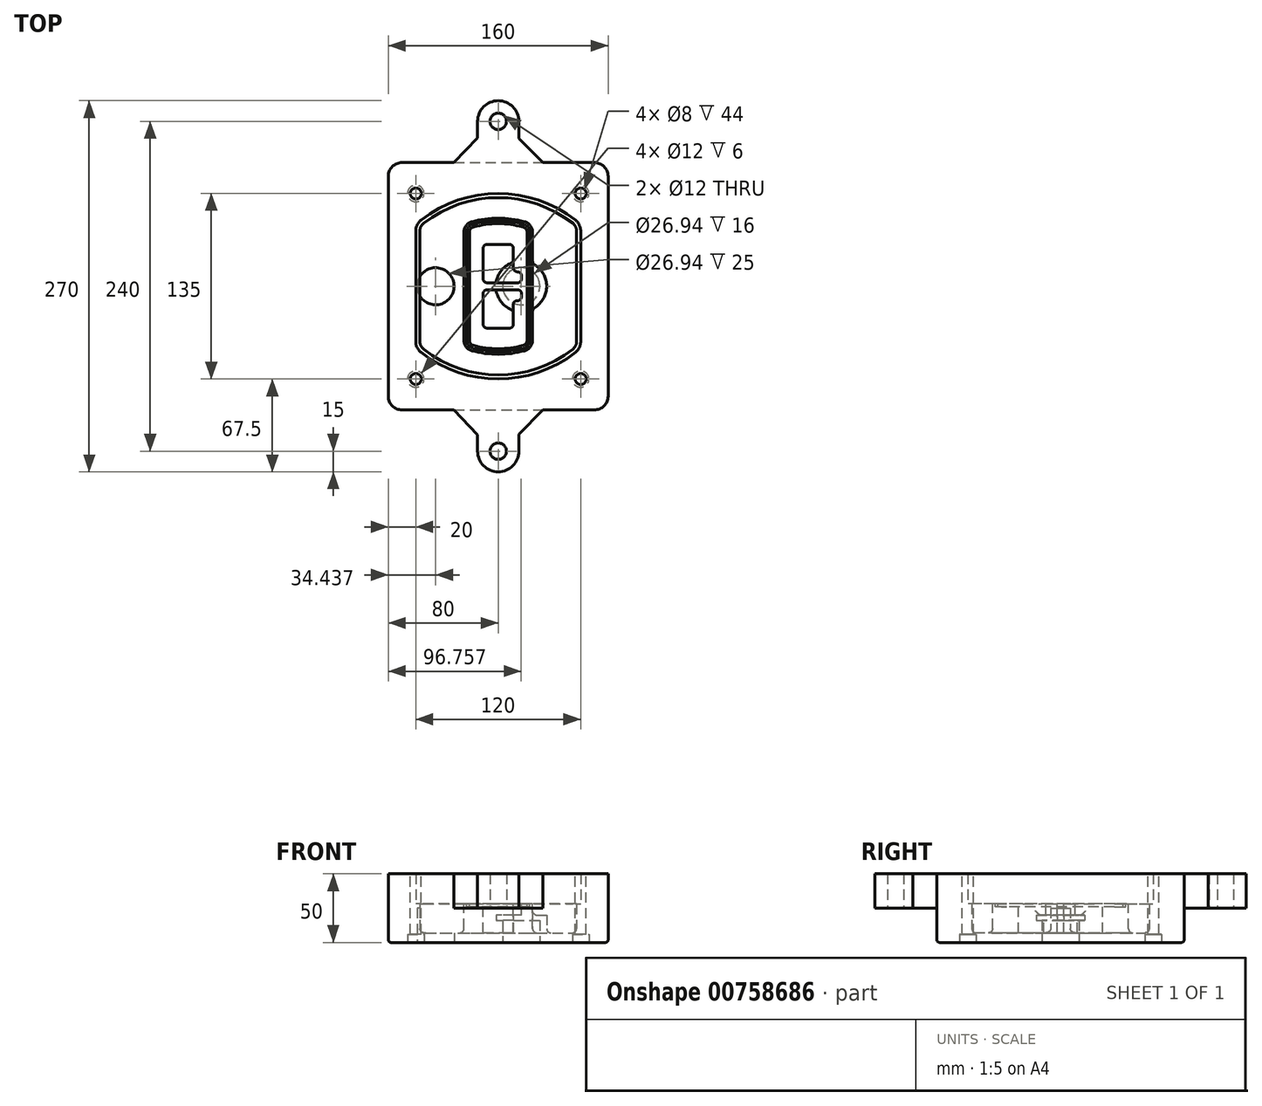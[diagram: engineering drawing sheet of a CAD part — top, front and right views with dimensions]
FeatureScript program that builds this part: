
annotation { "Feature Type Name" : "Feature", "Feature Type Description" : "" }
export const myFeature = defineFeature(function(context is Context, id is Id, definition is map)
    precondition{}
    {
        {
            var Q0;
            Q0=qCreatedBy(makeId("Top.planeOp"),FACE);
            var sketch = newSketch(context, id + "F0", { "sketchPlane" : qUnion([Q0])});
            skPoint(sketch, "E0.rect.middle", {"position": v(0, 0) * mm});
            skLineSegment(sketch, "E1.bottom", {"start": v(-70, -90) * mm, "end": v(70, -90) * mm});
            skLineSegment(sketch, "E1.top", {"start": v(-70, 90) * mm, "end": v(70, 90) * mm});
            skLineSegment(sketch, "E1.left", {"start": v(-80, -80) * mm, "end": v(-80, 80) * mm});
            skLineSegment(sketch, "E1.right", {"start": v(80, -80) * mm, "end": v(80, 80) * mm});
            skLineSegment(sketch, "E2", {"start": v(-80, 90) * mm, "end": v(80, -90) * mm, "construction": true});
            skLineSegment(sketch, "E3", {"start": v(80, 90) * mm, "end": v(-80, -90) * mm, "construction": true});
            skCircle(sketch, "E4", {"center": v(-60, 67.5) * mm, "radius": 4 * mm});
            skCircle(sketch, "E5", {"center": v(60, 67.5) * mm, "radius": 4 * mm});
            skCircle(sketch, "E6", {"center": v(60, -67.5) * mm, "radius": 4 * mm});
            skCircle(sketch, "E7", {"center": v(-60, -67.5) * mm, "radius": 4 * mm});
            skLineSegment(sketch, "E8", {"start": v(-60, 67.5) * mm, "end": v(60, 67.5) * mm, "construction": true});
            skLineSegment(sketch, "E9", {"start": v(60, 67.5) * mm, "end": v(60, -67.5) * mm, "construction": true});
            skLineSegment(sketch, "E10", {"start": v(60, -67.5) * mm, "end": v(-60, -67.5) * mm, "construction": true});
            skLineSegment(sketch, "E11", {"start": v(-60, -67.5) * mm, "end": v(-60, 67.5) * mm, "construction": true});
            skLineSegment(sketch, "E12", {"start": v(-60, 40.3) * mm, "end": v(-60, -40.3) * mm});
            skLineSegment(sketch, "E13", {"start": v(60, 40.3) * mm, "end": v(60, -40.3) * mm});
            skArc(sketch, "E14", {"start": v(56.15, 48.18) * mm, "mid": v(0, 67.5) * mm, "end": v(-56.15, 48.18) * mm});
            skArc(sketch, "E15", {"start": v(-56.15, -48.18) * mm, "mid": v(0, -67.5) * mm, "end": v(56.15, -48.18) * mm});
            skLineSegment(sketch, "E16", {"start": v(-60, 0) * mm, "end": v(60, 0) * mm, "construction": true});
            skPoint(sketch, "E17.visualSharp", {"position": v(-60, -45) * mm});
            skArc(sketch, "E17.filletArc", {"start": v(-60, -40.3) * mm, "mid": v(-58.99, -44.68) * mm, "end": v(-56.15, -48.18) * mm});
            skPoint(sketch, "E18.visualSharp", {"position": v(-60, 45) * mm});
            skArc(sketch, "E18.filletArc", {"start": v(-56.15, 48.18) * mm, "mid": v(-58.99, 44.68) * mm, "end": v(-60, 40.3) * mm});
            skPoint(sketch, "E19.visualSharp", {"position": v(60, 45) * mm});
            skArc(sketch, "E19.filletArc", {"start": v(60, 40.3) * mm, "mid": v(58.99, 44.68) * mm, "end": v(56.15, 48.18) * mm});
            skPoint(sketch, "E20.visualSharp", {"position": v(60, -45) * mm});
            skArc(sketch, "E20.filletArc", {"start": v(56.15, -48.18) * mm, "mid": v(58.99, -44.68) * mm, "end": v(60, -40.3) * mm});
            skPoint(sketch, "E21.visualSharp", {"position": v(-80, 90) * mm});
            skArc(sketch, "E21.filletArc", {"start": v(-70, 90) * mm, "mid": v(-77.07, 87.07) * mm, "end": v(-80, 80) * mm});
            skPoint(sketch, "E22.visualSharp", {"position": v(80, 90) * mm});
            skArc(sketch, "E22.filletArc", {"start": v(80, 80) * mm, "mid": v(77.07, 87.07) * mm, "end": v(70, 90) * mm});
            skPoint(sketch, "E23.visualSharp", {"position": v(80, -90) * mm});
            skArc(sketch, "E23.filletArc", {"start": v(70, -90) * mm, "mid": v(77.07, -87.07) * mm, "end": v(80, -80) * mm});
            skPoint(sketch, "E24.visualSharp", {"position": v(-80, -90) * mm});
            skArc(sketch, "E24.filletArc", {"start": v(-80, -80) * mm, "mid": v(-77.07, -87.07) * mm, "end": v(-70, -90) * mm});
            skArc(sketch, "E25.0", {"start": v(57, 40.3) * mm, "mid": v(56.3, 43.36) * mm, "end": v(54.3, 45.81) * mm});
            skLineSegment(sketch, "E25.1", {"start": v(57, 40.3) * mm, "end": v(57, -40.3) * mm});
            skArc(sketch, "E25.2", {"start": v(54.3, -45.81) * mm, "mid": v(56.3, -43.36) * mm, "end": v(57, -40.3) * mm});
            skArc(sketch, "E25.3", {"start": v(-54.3, -45.81) * mm, "mid": v(0, -64.5) * mm, "end": v(54.3, -45.81) * mm});
            skArc(sketch, "E25.4", {"start": v(-57, -40.3) * mm, "mid": v(-56.3, -43.36) * mm, "end": v(-54.3, -45.81) * mm});
            skArc(sketch, "E25.5", {"start": v(54.3, 45.81) * mm, "mid": v(0, 64.5) * mm, "end": v(-54.3, 45.81) * mm});
            skLineSegment(sketch, "E25.6", {"start": v(-57, 40.3) * mm, "end": v(-57, -40.3) * mm});
            skArc(sketch, "E25.7", {"start": v(-54.3, 45.81) * mm, "mid": v(-56.3, 43.36) * mm, "end": v(-57, 40.3) * mm});
            skArc(sketch, "E26.0", {"start": v(-58.62, 51.33) * mm, "mid": v(-62.58, 46.43) * mm, "end": v(-64, 40.3) * mm});
            skArc(sketch, "E26.1", {"start": v(58.62, 51.33) * mm, "mid": v(0, 71.5) * mm, "end": v(-58.62, 51.33) * mm});
            skArc(sketch, "E26.2", {"start": v(64, 40.3) * mm, "mid": v(62.58, 46.43) * mm, "end": v(58.62, 51.33) * mm});
            skLineSegment(sketch, "E26.3", {"start": v(64, 40.3) * mm, "end": v(64, -40.3) * mm});
            skArc(sketch, "E26.4", {"start": v(58.62, -51.33) * mm, "mid": v(62.58, -46.43) * mm, "end": v(64, -40.3) * mm});
            skLineSegment(sketch, "E26.5", {"start": v(-64, 40.3) * mm, "end": v(-64, -40.3) * mm});
            skArc(sketch, "E26.6", {"start": v(-58.62, -51.33) * mm, "mid": v(0, -71.5) * mm, "end": v(58.62, -51.33) * mm});
            skArc(sketch, "E26.7", {"start": v(-64, -40.3) * mm, "mid": v(-62.58, -46.43) * mm, "end": v(-58.62, -51.33) * mm});
            skSolve(sketch);
        }
        {
            var Q0;
            Q0=makeQuery(id+"F0.imprint","IMPRINT",FACE,{"disambiguationData":[TD([[makeQuery(id+"F0.imprint","IMPRINT",EDGE,{"derivedFrom":sQuery(id+"F0.wireOp",EDGE,"E1.bottom")}),1.0]])]});
            var Q1;
            Q1=makeQuery(id+"F0.imprint","IMPRINT",FACE,{"disambiguationData":[TD([[makeQuery(id+"F0.imprint","IMPRINT",EDGE,{"derivedFrom":sQuery(id+"F0.wireOp",EDGE,"E12")}),1.0]])]});
            var Q2;
            Q2=makeQuery(id+"F0.imprint","IMPRINT",FACE,{"disambiguationData":[TD([[makeQuery(id+"F0.imprint","IMPRINT",EDGE,{"derivedFrom":sQuery(id+"F0.wireOp",EDGE,"E25.0")}),1.0]])]});
            var Q3;
            Q3=makeQuery(id+"F0.imprint","IMPRINT",FACE,{"disambiguationData":[TD([[makeQuery(id+"F0.imprint","IMPRINT",EDGE,{"derivedFrom":sQuery(id+"F0.wireOp",EDGE,"E12")}),-1.0]])]});
            extrude(context, id + "F1", {"entities" : qUnion([Q0, Q1, Q2, Q3]), "oppositeDirection" : true, "depth" : 25 * mm});
        }
        {
            var Q0;
            Q0=makeQuery(id+"F0.imprint","IMPRINT",FACE,{"disambiguationData":[TD([[makeQuery(id+"F0.imprint","IMPRINT",EDGE,{"derivedFrom":sQuery(id+"F0.wireOp",EDGE,"E12")}),1.0]])]});
            extrude(context, id + "F2", {"entities" : qUnion([Q0]), "operationType" : NewBodyOperationType.ADD, "depth" : 3 * mm});
        }
        {
            var Q0;
            Q0=makeQuery(id+"F0.imprint","IMPRINT",FACE,{"disambiguationData":[TD([[makeQuery(id+"F0.imprint","IMPRINT",EDGE,{"derivedFrom":sQuery(id+"F0.wireOp",EDGE,"E25.0")}),1.0]])]});
            extrude(context, id + "F3", {"entities" : qUnion([Q0]), "operationType" : NewBodyOperationType.REMOVE, "oppositeDirection" : true, "depth" : 18 * mm});
        }
        {
            var Q0;
            Q0=makeQuery(id+"F2.opExtrude","CAP_FACE",FACE,{"disambiguationData":[OSD([sQuery(id+"F0.wireOp",EDGE,"E12"),sQuery(id+"F0.wireOp",EDGE,"E13"),sQuery(id+"F0.wireOp",EDGE,"E14"),sQuery(id+"F0.wireOp",EDGE,"E15"),sQuery(id+"F0.wireOp",EDGE,"E17.filletArc"),sQuery(id+"F0.wireOp",EDGE,"E18.filletArc"),sQuery(id+"F0.wireOp",EDGE,"E19.filletArc"),sQuery(id+"F0.wireOp",EDGE,"E20.filletArc"),sQuery(id+"F0.wireOp",EDGE,"E25.0"),sQuery(id+"F0.wireOp",EDGE,"E25.1"),sQuery(id+"F0.wireOp",EDGE,"E25.2"),sQuery(id+"F0.wireOp",EDGE,"E25.3"),sQuery(id+"F0.wireOp",EDGE,"E25.4"),sQuery(id+"F0.wireOp",EDGE,"E25.5"),sQuery(id+"F0.wireOp",EDGE,"E25.6"),sQuery(id+"F0.wireOp",EDGE,"E25.7")])],"isStart":false});
            var sketch = newSketch(context, id + "F4", { "sketchPlane" : qUnion([Q0])});
            skArc(sketch, "E27.0", {"start": v(-19.08, -46.97) * mm, "mid": v(0, -49.5) * mm, "end": v(19.08, -46.97) * mm});
            skArc(sketch, "E28.0", {"start": v(19.08, 46.97) * mm, "mid": v(0, 49.5) * mm, "end": v(-19.08, 46.97) * mm});
            skLineSegment(sketch, "E29", {"start": v(-25, 39.25) * mm, "end": v(-25, -39.25) * mm});
            skLineSegment(sketch, "E30", {"start": v(25, 39.25) * mm, "end": v(25, -39.25) * mm});
            skLineSegment(sketch, "E31", {"start": v(-25, 45.1) * mm, "end": v(25, 45.1) * mm, "construction": true});
            skLineSegment(sketch, "E32", {"start": v(-25, -45.1) * mm, "end": v(25, -45.1) * mm, "construction": true});
            skPoint(sketch, "E33.visualSharp", {"position": v(-25, 45.1) * mm});
            skArc(sketch, "E33.filletArc", {"start": v(-19.08, 46.97) * mm, "mid": v(-23.35, 44.11) * mm, "end": v(-25, 39.25) * mm});
            skPoint(sketch, "E34.visualSharp", {"position": v(25, 45.1) * mm});
            skArc(sketch, "E34.filletArc", {"start": v(25, 39.25) * mm, "mid": v(23.35, 44.11) * mm, "end": v(19.08, 46.97) * mm});
            skPoint(sketch, "E35.visualSharp", {"position": v(25, -45.1) * mm});
            skArc(sketch, "E35.filletArc", {"start": v(19.08, -46.97) * mm, "mid": v(23.35, -44.11) * mm, "end": v(25, -39.25) * mm});
            skPoint(sketch, "E36.visualSharp", {"position": v(-25, -45.1) * mm});
            skArc(sketch, "E36.filletArc", {"start": v(-25, -39.25) * mm, "mid": v(-23.35, -44.11) * mm, "end": v(-19.08, -46.97) * mm});
            skArc(sketch, "E37.0", {"start": v(54.3, 45.81) * mm, "mid": v(0, 64.5) * mm, "end": v(-54.3, 45.81) * mm});
            skArc(sketch, "E37.1", {"start": v(-54.3, 45.81) * mm, "mid": v(-56.3, 43.36) * mm, "end": v(-57, 40.3) * mm});
            skLineSegment(sketch, "E37.2", {"start": v(-57, 40.3) * mm, "end": v(-57, -40.3) * mm});
            skArc(sketch, "E37.3", {"start": v(-57, -40.3) * mm, "mid": v(-56.3, -43.36) * mm, "end": v(-54.3, -45.81) * mm});
            skArc(sketch, "E37.4", {"start": v(-54.3, -45.81) * mm, "mid": v(0, -64.5) * mm, "end": v(54.3, -45.81) * mm});
            skArc(sketch, "E37.5", {"start": v(54.3, -45.81) * mm, "mid": v(56.3, -43.36) * mm, "end": v(57, -40.3) * mm});
            skLineSegment(sketch, "E37.6", {"start": v(57, 40.3) * mm, "end": v(57, -40.3) * mm});
            skArc(sketch, "E37.7", {"start": v(57, 40.3) * mm, "mid": v(56.3, 43.36) * mm, "end": v(54.3, 45.81) * mm});
            skLineSegment(sketch, "E38.0", {"start": v(23, 39.25) * mm, "end": v(23, -39.25) * mm});
            skArc(sketch, "E38.1", {"start": v(18.56, -45.04) * mm, "mid": v(21.76, -42.9) * mm, "end": v(23, -39.25) * mm});
            skArc(sketch, "E38.2", {"start": v(-18.56, -45.04) * mm, "mid": v(0, -47.5) * mm, "end": v(18.56, -45.04) * mm});
            skArc(sketch, "E38.3", {"start": v(-23, -39.25) * mm, "mid": v(-21.76, -42.9) * mm, "end": v(-18.56, -45.04) * mm});
            skLineSegment(sketch, "E38.4", {"start": v(-23, 39.25) * mm, "end": v(-23, -39.25) * mm});
            skArc(sketch, "E38.5", {"start": v(23, 39.25) * mm, "mid": v(21.76, 42.9) * mm, "end": v(18.56, 45.04) * mm});
            skArc(sketch, "E38.6", {"start": v(-18.56, 45.04) * mm, "mid": v(-21.76, 42.9) * mm, "end": v(-23, 39.25) * mm});
            skArc(sketch, "E38.7", {"start": v(18.56, 45.04) * mm, "mid": v(0, 47.5) * mm, "end": v(-18.56, 45.04) * mm});
            skArc(sketch, "E39.0", {"start": v(21, 39.25) * mm, "mid": v(20.18, 41.68) * mm, "end": v(18.04, 43.1) * mm});
            skLineSegment(sketch, "E39.1", {"start": v(21, 39.25) * mm, "end": v(21, -39.25) * mm});
            skArc(sketch, "E39.2", {"start": v(18.04, -43.1) * mm, "mid": v(20.18, -41.68) * mm, "end": v(21, -39.25) * mm});
            skArc(sketch, "E39.3", {"start": v(-18.04, -43.1) * mm, "mid": v(0, -45.5) * mm, "end": v(18.04, -43.1) * mm});
            skArc(sketch, "E39.4", {"start": v(-21, -39.25) * mm, "mid": v(-20.18, -41.68) * mm, "end": v(-18.04, -43.1) * mm});
            skArc(sketch, "E39.5", {"start": v(18.04, 43.1) * mm, "mid": v(0, 45.5) * mm, "end": v(-18.04, 43.1) * mm});
            skLineSegment(sketch, "E39.6", {"start": v(-21, 39.25) * mm, "end": v(-21, -39.25) * mm});
            skArc(sketch, "E39.7", {"start": v(-18.04, 43.1) * mm, "mid": v(-20.18, 41.68) * mm, "end": v(-21, 39.25) * mm});
            skLineSegment(sketch, "E40", {"start": v(-25, 0) * mm, "end": v(25, 0) * mm, "construction": true});
            skLineSegment(sketch, "E41", {"start": v(-11, 5.5) * mm, "end": v(-11, 27.5) * mm});
            skLineSegment(sketch, "E42", {"start": v(-8, 30.5) * mm, "end": v(8, 30.5) * mm});
            skLineSegment(sketch, "E43", {"start": v(11, 27.5) * mm, "end": v(11, 13.5) * mm});
            skLineSegment(sketch, "E44", {"start": v(14, 10.5) * mm, "end": v(14, 10.5) * mm});
            skLineSegment(sketch, "E45", {"start": v(17, 7.5) * mm, "end": v(17, 5.5) * mm});
            skLineSegment(sketch, "E46", {"start": v(14, 2.5) * mm, "end": v(-8, 2.5) * mm});
            skPoint(sketch, "E47.visualSharp", {"position": v(-11, 30.5) * mm});
            skArc(sketch, "E47.filletArc", {"start": v(-8, 30.5) * mm, "mid": v(-10.12, 29.62) * mm, "end": v(-11, 27.5) * mm});
            skPoint(sketch, "E48.visualSharp", {"position": v(11, 30.5) * mm});
            skArc(sketch, "E48.filletArc", {"start": v(11, 27.5) * mm, "mid": v(10.12, 29.62) * mm, "end": v(8, 30.5) * mm});
            skPoint(sketch, "E49.visualSharp", {"position": v(11, 10.5) * mm});
            skArc(sketch, "E49.filletArc", {"start": v(11, 13.5) * mm, "mid": v(11.88, 11.38) * mm, "end": v(14, 10.5) * mm});
            skPoint(sketch, "E50.visualSharp", {"position": v(17, 10.5) * mm});
            skArc(sketch, "E50.filletArc", {"start": v(17, 7.5) * mm, "mid": v(16.12, 9.62) * mm, "end": v(14, 10.5) * mm});
            skPoint(sketch, "E51.visualSharp", {"position": v(17, 2.5) * mm});
            skArc(sketch, "E51.filletArc", {"start": v(14, 2.5) * mm, "mid": v(16.12, 3.38) * mm, "end": v(17, 5.5) * mm});
            skPoint(sketch, "E52.visualSharp", {"position": v(-11, 2.5) * mm});
            skArc(sketch, "E52.filletArc", {"start": v(-11, 5.5) * mm, "mid": v(-10.12, 3.38) * mm, "end": v(-8, 2.5) * mm});
            skLineSegment(sketch, "E53.0.MirrorCS", {"start": v(14, -2.5) * mm, "end": v(-8, -2.5) * mm});
            skArc(sketch, "E54.0.MirrorCS", {"start": v(-11, -5.5) * mm, "mid": v(-10.12, -3.38) * mm, "end": v(-8, -2.5) * mm});
            skLineSegment(sketch, "E55.0.MirrorCS", {"start": v(-11, -5.5) * mm, "end": v(-11, -27.5) * mm});
            skArc(sketch, "E56.0.MirrorCS", {"start": v(-8, -30.5) * mm, "mid": v(-10.12, -29.62) * mm, "end": v(-11, -27.5) * mm});
            skLineSegment(sketch, "E57.0.MirrorCS", {"start": v(-8, -30.5) * mm, "end": v(8, -30.5) * mm});
            skArc(sketch, "E58.0.MirrorCS", {"start": v(11, -27.5) * mm, "mid": v(10.12, -29.62) * mm, "end": v(8, -30.5) * mm});
            skLineSegment(sketch, "E59.0.MirrorCS", {"start": v(11, -27.5) * mm, "end": v(11, -13.5) * mm});
            skArc(sketch, "E60.0.MirrorCS", {"start": v(11, -13.5) * mm, "mid": v(11.88, -11.38) * mm, "end": v(14, -10.5) * mm});
            skArc(sketch, "E61.0.MirrorCS", {"start": v(17, -7.5) * mm, "mid": v(16.12, -9.62) * mm, "end": v(14, -10.5) * mm});
            skLineSegment(sketch, "E62.0.MirrorCS", {"start": v(17, -7.5) * mm, "end": v(17, -5.5) * mm});
            skArc(sketch, "E63.0.MirrorCS", {"start": v(14, -2.5) * mm, "mid": v(16.12, -3.38) * mm, "end": v(17, -5.5) * mm});
            skSolve(sketch);
        }
        {
            var Q0;
            Q0=makeQuery(id+"F4.imprint","IMPRINT",FACE,{"disambiguationData":[TD([[makeQuery(id+"F4.imprint","IMPRINT",EDGE,{"derivedFrom":sQuery(id+"F4.wireOp",EDGE,"E27.0")}),1.0]])]});
            var Q1;
            Q1=makeQuery(id+"F4.imprint","IMPRINT",FACE,{"disambiguationData":[TD([[makeQuery(id+"F4.imprint","IMPRINT",EDGE,{"derivedFrom":sQuery(id+"F4.wireOp",EDGE,"E38.0")}),-1.0]])]});
            var Q2;
            Q2=makeQuery(id+"F4.imprint","IMPRINT",FACE,{"disambiguationData":[TD([[makeQuery(id+"F4.imprint","IMPRINT",EDGE,{"derivedFrom":sQuery(id+"F4.wireOp",EDGE,"E39.0")}),1.0]])]});
            extrude(context, id + "F5", {"entities" : qUnion([Q0, Q1, Q2]), "operationType" : NewBodyOperationType.ADD, "endBound" : BoundingType.UP_TO_NEXT, "oppositeDirection" : true, "depth" : 25 * mm});
        }
        {
            var Q0;
            Q0=makeQuery(id+"F4.imprint","IMPRINT",FACE,{"disambiguationData":[TD([[makeQuery(id+"F4.imprint","IMPRINT",EDGE,{"derivedFrom":sQuery(id+"F4.wireOp",EDGE,"E38.0")}),-1.0]])]});
            extrude(context, id + "F6", {"entities" : qUnion([Q0]), "operationType" : NewBodyOperationType.REMOVE, "oppositeDirection" : true, "depth" : 2 * mm});
        }
        {
            var Q0;
            Q0=makeQuery(id+"F1.opExtrude","CAP_FACE",FACE,{"disambiguationData":[OSD([sQuery(id+"F0.wireOp",EDGE,"E1.bottom"),sQuery(id+"F0.wireOp",EDGE,"E1.top"),sQuery(id+"F0.wireOp",EDGE,"E1.left"),sQuery(id+"F0.wireOp",EDGE,"E1.right"),sQuery(id+"F0.wireOp",EDGE,"E4"),sQuery(id+"F0.wireOp",EDGE,"E5"),sQuery(id+"F0.wireOp",EDGE,"E6"),sQuery(id+"F0.wireOp",EDGE,"E7"),sQuery(id+"F0.wireOp",EDGE,"E21.filletArc"),sQuery(id+"F0.wireOp",EDGE,"E22.filletArc"),sQuery(id+"F0.wireOp",EDGE,"E23.filletArc"),sQuery(id+"F0.wireOp",EDGE,"E24.filletArc")])],"isStart":false});
            var sketch = newSketch(context, id + "F7", { "sketchPlane" : qUnion([Q0])});
            skCircle(sketch, "E64", {"center": v(16.76, 0) * mm, "radius": 13.47 * mm});
            skCircle(sketch, "E65", {"center": v(-45.56, 0) * mm, "radius": 13.47 * mm});
            skLineSegment(sketch, "E66", {"start": v(80, 0) * mm, "end": v(-80, 0) * mm});
            skCircle(sketch, "E67", {"center": v(16.76, 0) * mm, "radius": 18.47 * mm});
            skCircle(sketch, "E68", {"center": v(60, -67.5) * mm, "radius": 6 * mm});
            skCircle(sketch, "E69", {"center": v(-60, -67.5) * mm, "radius": 6 * mm});
            skCircle(sketch, "E70", {"center": v(-60, 67.5) * mm, "radius": 6 * mm});
            skCircle(sketch, "E71", {"center": v(60, 67.5) * mm, "radius": 6 * mm});
            skSolve(sketch);
        }
        {
            var Q0;
            {var subQ1=sQuery(id+"F7.wireOp",EDGE,"E66");var subQ4=sQuery(id+"F7.wireOp",EDGE,"E64");var subQ6=makeQuery(id+"F7.imprint","INTERSECT",VERTEX,{"disambiguationData":[OD(0.0)],"derivedFrom":[subQ4,subQ1]});Q0=makeQuery(id+"F7.imprint","IMPRINT",FACE,{"disambiguationData":[TD([[makeQuery(id+"F7.imprint","IMPRINT",EDGE,{"disambiguationData":[TD([[subQ6,-1.0]])],"derivedFrom":subQ4}),-1.0]])]});}
            var Q1;
            {var subQ0=sQuery(id+"F7.wireOp",EDGE,"E66");var subQ1=sQuery(id+"F7.wireOp",EDGE,"E64");var subQ3=makeQuery(id+"F7.imprint","INTERSECT",VERTEX,{"disambiguationData":[OD(0.0)],"derivedFrom":[subQ1,subQ0]});Q1=makeQuery(id+"F7.imprint","IMPRINT",FACE,{"disambiguationData":[TD([[makeQuery(id+"F7.imprint","IMPRINT",EDGE,{"disambiguationData":[TD([[subQ3,-1.0]])],"derivedFrom":subQ1}),1.0]])]});}
            var Q2;
            {var subQ0=sQuery(id+"F7.wireOp",EDGE,"E66");var subQ1=sQuery(id+"F7.wireOp",EDGE,"E64");var subQ3=makeQuery(id+"F7.imprint","INTERSECT",VERTEX,{"disambiguationData":[OD(0.0)],"derivedFrom":[subQ1,subQ0]});Q2=makeQuery(id+"F7.imprint","IMPRINT",FACE,{"disambiguationData":[TD([[makeQuery(id+"F7.imprint","IMPRINT",EDGE,{"disambiguationData":[TD([[subQ3,1.0]])],"derivedFrom":subQ1}),1.0]])]});}
            var Q3;
            {var subQ1=sQuery(id+"F7.wireOp",EDGE,"E66");var subQ4=sQuery(id+"F7.wireOp",EDGE,"E64");var subQ6=makeQuery(id+"F7.imprint","INTERSECT",VERTEX,{"disambiguationData":[OD(0.0)],"derivedFrom":[subQ4,subQ1]});Q3=makeQuery(id+"F7.imprint","IMPRINT",FACE,{"disambiguationData":[TD([[makeQuery(id+"F7.imprint","IMPRINT",EDGE,{"disambiguationData":[TD([[subQ6,1.0]])],"derivedFrom":subQ4}),-1.0]])]});}
            extrude(context, id + "F8", {"entities" : qUnion([Q0, Q1, Q2, Q3]), "operationType" : NewBodyOperationType.ADD, "oppositeDirection" : true, "depth" : 20 * mm});
        }
        {
            var Q0;
            {var subQ0=sQuery(id+"F7.wireOp",EDGE,"E66");var subQ1=sQuery(id+"F7.wireOp",EDGE,"E64");var subQ3=makeQuery(id+"F7.imprint","INTERSECT",VERTEX,{"disambiguationData":[OD(0.0)],"derivedFrom":[subQ1,subQ0]});Q0=makeQuery(id+"F7.imprint","IMPRINT",FACE,{"disambiguationData":[TD([[makeQuery(id+"F7.imprint","IMPRINT",EDGE,{"disambiguationData":[TD([[subQ3,-1.0]])],"derivedFrom":subQ1}),1.0]])]});}
            var Q1;
            {var subQ0=sQuery(id+"F7.wireOp",EDGE,"E66");var subQ1=sQuery(id+"F7.wireOp",EDGE,"E64");var subQ3=makeQuery(id+"F7.imprint","INTERSECT",VERTEX,{"disambiguationData":[OD(0.0)],"derivedFrom":[subQ1,subQ0]});Q1=makeQuery(id+"F7.imprint","IMPRINT",FACE,{"disambiguationData":[TD([[makeQuery(id+"F7.imprint","IMPRINT",EDGE,{"disambiguationData":[TD([[subQ3,1.0]])],"derivedFrom":subQ1}),1.0]])]});}
            extrude(context, id + "F9", {"entities" : qUnion([Q0, Q1]), "operationType" : NewBodyOperationType.REMOVE, "oppositeDirection" : true, "depth" : 16 * mm});
        }
        {
            var Q0;
            {var subQ0=sQuery(id+"F7.wireOp",EDGE,"E66");var subQ1=sQuery(id+"F7.wireOp",EDGE,"E65");var subQ3=makeQuery(id+"F7.imprint","INTERSECT",VERTEX,{"disambiguationData":[OD(0.0)],"derivedFrom":[subQ1,subQ0]});Q0=makeQuery(id+"F7.imprint","IMPRINT",FACE,{"disambiguationData":[TD([[makeQuery(id+"F7.imprint","IMPRINT",EDGE,{"disambiguationData":[TD([[subQ3,-1.0]])],"derivedFrom":subQ1}),1.0]])]});}
            var Q1;
            {var subQ0=sQuery(id+"F7.wireOp",EDGE,"E66");var subQ1=sQuery(id+"F7.wireOp",EDGE,"E65");var subQ3=makeQuery(id+"F7.imprint","INTERSECT",VERTEX,{"disambiguationData":[OD(0.0)],"derivedFrom":[subQ1,subQ0]});Q1=makeQuery(id+"F7.imprint","IMPRINT",FACE,{"disambiguationData":[TD([[makeQuery(id+"F7.imprint","IMPRINT",EDGE,{"disambiguationData":[TD([[subQ3,1.0]])],"derivedFrom":subQ1}),1.0]])]});}
            extrude(context, id + "F10", {"entities" : qUnion([Q0, Q1]), "operationType" : NewBodyOperationType.REMOVE, "oppositeDirection" : true, "depth" : 25 * mm});
        }
        {
            var Q0;
            Q0=makeQuery(id+"F7.imprint","IMPRINT",FACE,{"disambiguationData":[TD([[makeQuery(id+"F7.imprint","IMPRINT",EDGE,{"derivedFrom":sQuery(id+"F7.wireOp",EDGE,"E68")}),1.0]])]});
            var Q1;
            Q1=makeQuery(id+"F7.imprint","IMPRINT",FACE,{"disambiguationData":[TD([[makeQuery(id+"F7.imprint","IMPRINT",EDGE,{"derivedFrom":makeQuery(id+"F1.opExtrude","CAP_EDGE",EDGE,{"disambiguationData":[OSD([sQuery(id+"F0.wireOp",EDGE,"E5")])],"isStart":false})}),-1.0]])]});
            var Q2;
            Q2=makeQuery(id+"F7.imprint","IMPRINT",FACE,{"disambiguationData":[TD([[makeQuery(id+"F7.imprint","IMPRINT",EDGE,{"derivedFrom":sQuery(id+"F7.wireOp",EDGE,"E69")}),1.0]])]});
            var Q3;
            Q3=makeQuery(id+"F7.imprint","IMPRINT",FACE,{"disambiguationData":[TD([[makeQuery(id+"F7.imprint","IMPRINT",EDGE,{"derivedFrom":makeQuery(id+"F1.opExtrude","CAP_EDGE",EDGE,{"disambiguationData":[OSD([sQuery(id+"F0.wireOp",EDGE,"E4")])],"isStart":false})}),-1.0]])]});
            var Q4;
            Q4=makeQuery(id+"F7.imprint","IMPRINT",FACE,{"disambiguationData":[TD([[makeQuery(id+"F7.imprint","IMPRINT",EDGE,{"derivedFrom":sQuery(id+"F7.wireOp",EDGE,"E70")}),1.0]])]});
            var Q5;
            Q5=makeQuery(id+"F7.imprint","IMPRINT",FACE,{"disambiguationData":[TD([[makeQuery(id+"F7.imprint","IMPRINT",EDGE,{"derivedFrom":makeQuery(id+"F1.opExtrude","CAP_EDGE",EDGE,{"disambiguationData":[OSD([sQuery(id+"F0.wireOp",EDGE,"E7")])],"isStart":false})}),-1.0]])]});
            var Q6;
            Q6=makeQuery(id+"F7.imprint","IMPRINT",FACE,{"disambiguationData":[TD([[makeQuery(id+"F7.imprint","IMPRINT",EDGE,{"derivedFrom":sQuery(id+"F7.wireOp",EDGE,"E71")}),1.0]])]});
            var Q7;
            Q7=makeQuery(id+"F7.imprint","IMPRINT",FACE,{"disambiguationData":[TD([[makeQuery(id+"F7.imprint","IMPRINT",EDGE,{"derivedFrom":makeQuery(id+"F1.opExtrude","CAP_EDGE",EDGE,{"disambiguationData":[OSD([sQuery(id+"F0.wireOp",EDGE,"E6")])],"isStart":false})}),-1.0]])]});
            extrude(context, id + "F11", {"entities" : qUnion([Q0, Q1, Q2, Q3, Q4, Q5, Q6, Q7]), "operationType" : NewBodyOperationType.REMOVE, "oppositeDirection" : true, "depth" : 6 * mm});
        }
        {
            var Q0;
            Q0=makeQuery(id+"F9.boolean.opBoolean","COPY",FACE,{"derivedFrom":makeQuery(id+"F9.opExtrude","CAP_FACE",FACE,{"disambiguationData":[OSD([sQuery(id+"F7.wireOp",EDGE,"E64")])],"isStart":false})});
            var sketch = newSketch(context, id + "F12", { "sketchPlane" : qUnion([Q0])});
            skArc(sketch, "E72.0", {"start": v(11, 17.55) * mm, "mid": v(2.57, 11.82) * mm, "end": v(-1.54, 2.5) * mm});
            skArc(sketch, "E72.1", {"start": v(-1.54, -2.5) * mm, "mid": v(2.57, -11.82) * mm, "end": v(11, -17.55) * mm});
            skLineSegment(sketch, "E73", {"start": v(-1.54, -2.5) * mm, "end": v(14, -2.5) * mm});
            skLineSegment(sketch, "E74.0", {"start": v(14, 2.5) * mm, "end": v(-1.54, 2.5) * mm});
            skArc(sketch, "E74.1", {"start": v(14, 2.5) * mm, "mid": v(16.12, 3.38) * mm, "end": v(17, 5.5) * mm});
            skLineSegment(sketch, "E74.2", {"start": v(17, 7.5) * mm, "end": v(17, 5.5) * mm});
            skArc(sketch, "E74.3", {"start": v(17, 7.5) * mm, "mid": v(16.12, 9.62) * mm, "end": v(14, 10.5) * mm});
            skArc(sketch, "E74.4", {"start": v(11, 13.5) * mm, "mid": v(11.88, 11.38) * mm, "end": v(14, 10.5) * mm});
            skLineSegment(sketch, "E74.5", {"start": v(11, 17.55) * mm, "end": v(11, 13.5) * mm});
            skLineSegment(sketch, "E74.7", {"start": v(14, -2.5) * mm, "end": v(-1.54, -2.5) * mm});
            skArc(sketch, "E74.8", {"start": v(14, -2.5) * mm, "mid": v(16.12, -3.38) * mm, "end": v(17, -5.5) * mm});
            skLineSegment(sketch, "E74.9", {"start": v(17, -7.5) * mm, "end": v(17, -5.5) * mm});
            skArc(sketch, "E74.10", {"start": v(17, -7.5) * mm, "mid": v(16.12, -9.62) * mm, "end": v(14, -10.5) * mm});
            skArc(sketch, "E74.11", {"start": v(11, -13.5) * mm, "mid": v(11.88, -11.38) * mm, "end": v(14, -10.5) * mm});
            skLineSegment(sketch, "E74.12", {"start": v(11, -17.55) * mm, "end": v(11, -13.5) * mm});
            skPoint(sketch, "E75.orphan", {"position": v(11, -27.5) * mm});
            skPoint(sketch, "E76.orphan", {"position": v(-8, -2.5) * mm});
            skPoint(sketch, "E77.orphan", {"position": v(-8, 2.5) * mm});
            skPoint(sketch, "E78.orphan", {"position": v(11, 27.5) * mm});
            skSolve(sketch);
        }
        {
            var Q0;
            {var subQ7=sQuery(id+"F12.wireOp",EDGE,"E72.0");var subQ14=sQuery(id+"F12.wireOp",EDGE,"E72.1");var subQ16=sQuery(id+"F12.wireOp",EDGE,"E74.1");var subQ18=sQuery(id+"F12.wireOp",EDGE,"E74.8");Q0=qUnion([makeQuery(id+"F12.imprint","IMPRINT",FACE,{"disambiguationData":[TD([[makeQuery(id+"F12.imprint","IMPRINT",EDGE,{"derivedFrom":subQ7}),1.0]])]}),makeQuery(id+"F12.imprint","IMPRINT",FACE,{"disambiguationData":[TD([[makeQuery(id+"F12.imprint","IMPRINT",EDGE,{"derivedFrom":subQ14}),1.0]])]}),makeQuery(id+"F12.imprint","IMPRINT",FACE,{"disambiguationData":[TD([[makeQuery(id+"F12.imprint","IMPRINT",EDGE,{"derivedFrom":subQ16}),1.0]])]}),makeQuery(id+"F12.imprint","IMPRINT",FACE,{"disambiguationData":[TD([[makeQuery(id+"F12.imprint","IMPRINT",EDGE,{"derivedFrom":subQ18}),-1.0]])]})]);}
            var Q1;
            Q1=makeQuery(id+"F5.boolean.opBoolean","SPLIT",FACE,{"disambiguationData":[TD([makeQuery(id+"F5.opExtrude","SWEPT_FACE",FACE,{"disambiguationData":[OSD([sQuery(id+"F4.wireOp",EDGE,"E41")])]})])],"derivedFrom":makeQuery(id+"F3.boolean.opBoolean","COPY",FACE,{"derivedFrom":makeQuery(id+"F3.opExtrude","CAP_FACE",FACE,{"disambiguationData":[OSD([sQuery(id+"F0.wireOp",EDGE,"E25.0"),sQuery(id+"F0.wireOp",EDGE,"E25.1"),sQuery(id+"F0.wireOp",EDGE,"E25.2"),sQuery(id+"F0.wireOp",EDGE,"E25.3"),sQuery(id+"F0.wireOp",EDGE,"E25.4"),sQuery(id+"F0.wireOp",EDGE,"E25.5"),sQuery(id+"F0.wireOp",EDGE,"E25.6"),sQuery(id+"F0.wireOp",EDGE,"E25.7")])],"isStart":false})})});
            extrude(context, id + "F13", {"entities" : qUnion([Q0]), "operationType" : NewBodyOperationType.REMOVE, "endBound" : BoundingType.UP_TO_SURFACE, "endBoundEntityFace" : qUnion([Q1]), "depth" : 25 * mm});
        }
        {
            var Q0;
            Q0=makeQuery(id+"F3.boolean.opBoolean","COPY",EDGE,{"derivedFrom":makeQuery(id+"F3.opExtrude","CAP_EDGE",EDGE,{"disambiguationData":[OSD([sQuery(id+"F0.wireOp",EDGE,"E25.6")])],"isStart":false})});
            var Q1;
            Q1=makeQuery(id+"F8.boolean.opBoolean","INTERSECT",EDGE,{"derivedFrom":[makeQuery(id+"F5.opExtrude","SWEPT_FACE",FACE,{"disambiguationData":[OSD([sQuery(id+"F4.wireOp",EDGE,"E30")])]}),makeQuery(id+"F8.opExtrude","CAP_FACE",FACE,{"disambiguationData":[OSD([sQuery(id+"F7.wireOp",EDGE,"E67")])],"isStart":false})]});
            var Q2;
            Q2=makeQuery(id+"F8.boolean.opBoolean","INTERSECT",EDGE,{"disambiguationData":[OD(1.0)],"derivedFrom":[makeQuery(id+"F5.opExtrude","SWEPT_FACE",FACE,{"disambiguationData":[OSD([sQuery(id+"F4.wireOp",EDGE,"E30")])]}),makeQuery(id+"F8.opExtrude","SWEPT_FACE",FACE,{"disambiguationData":[OSD([sQuery(id+"F7.wireOp",EDGE,"E67")])]})]});
            var Q3;
            {var subQ0=sQuery(id+"F4.wireOp",EDGE,"E30");Q3=makeQuery(id+"F8.boolean.opBoolean","SPLIT",EDGE,{"disambiguationData":[TD([makeQuery(id+"F5.opExtrude","SWEPT_FACE",FACE,{"disambiguationData":[OSD([sQuery(id+"F4.wireOp",EDGE,"E35.filletArc")])]})])],"derivedFrom":makeQuery(id+"F5.opExtrude","CAP_EDGE",EDGE,{"disambiguationData":[OSD([subQ0])],"isStart":false})});}
            var Q4;
            {var subQ0=sQuery(id+"F0.wireOp",EDGE,"E25.7");var subQ1=sQuery(id+"F0.wireOp",EDGE,"E25.1");var subQ2=sQuery(id+"F0.wireOp",EDGE,"E25.6");var subQ3=sQuery(id+"F0.wireOp",EDGE,"E25.5");var subQ4=sQuery(id+"F0.wireOp",EDGE,"E25.4");var subQ5=sQuery(id+"F0.wireOp",EDGE,"E25.0");var subQ6=sQuery(id+"F0.wireOp",EDGE,"E25.2");var subQ7=sQuery(id+"F0.wireOp",EDGE,"E25.3");Q4=makeQuery(id+"F8.boolean.opBoolean","INTERSECT",EDGE,{"derivedFrom":[makeQuery(id+"F5.boolean.opBoolean","SPLIT",FACE,{"disambiguationData":[TD([makeQuery(id+"F2.opExtrude","SWEPT_FACE",FACE,{"disambiguationData":[OSD([subQ5])]})])],"derivedFrom":makeQuery(id+"F3.boolean.opBoolean","COPY",FACE,{"derivedFrom":makeQuery(id+"F3.opExtrude","CAP_FACE",FACE,{"disambiguationData":[OSD([subQ5,subQ1,subQ6,subQ7,subQ4,subQ3,subQ2,subQ0])],"isStart":false})})}),makeQuery(id+"F8.opExtrude","SWEPT_FACE",FACE,{"disambiguationData":[OSD([sQuery(id+"F7.wireOp",EDGE,"E67")])]})]});}
            var Q5;
            Q5=makeQuery(id+"F8.boolean.opBoolean","INTERSECT",EDGE,{"disambiguationData":[OD(0.0)],"derivedFrom":[makeQuery(id+"F5.opExtrude","SWEPT_FACE",FACE,{"disambiguationData":[OSD([sQuery(id+"F4.wireOp",EDGE,"E30")])]}),makeQuery(id+"F8.opExtrude","SWEPT_FACE",FACE,{"disambiguationData":[OSD([sQuery(id+"F7.wireOp",EDGE,"E67")])]})]});
            fillet(context, id + "F14", {"entities" : qUnion([Q0, Q1, Q2, Q3, Q4, Q5]), "radius" : 3 * mm, "tangentPropagation" : true, "allowEdgeOverflow" : false});
        }
        {
            var Q0;
            Q0=makeQuery(id+"F1.opExtrude","CAP_EDGE",EDGE,{"disambiguationData":[OSD([sQuery(id+"F0.wireOp",EDGE,"E1.bottom")])],"isStart":false});
            fillet(context, id + "F15", {"entities" : qUnion([Q0]), "radius" : 2 * mm, "tangentPropagation" : true, "allowEdgeOverflow" : false});
        }
        {
            var Q0;
            {var subQ0=sQuery(id+"F0.wireOp",EDGE,"E21.filletArc");var subQ1=sQuery(id+"F0.wireOp",EDGE,"E7");var subQ2=sQuery(id+"F0.wireOp",EDGE,"E6");var subQ3=sQuery(id+"F0.wireOp",EDGE,"E5");var subQ4=sQuery(id+"F0.wireOp",EDGE,"E4");var subQ5=sQuery(id+"F0.wireOp",EDGE,"E22.filletArc");var subQ6=sQuery(id+"F0.wireOp",EDGE,"E1.bottom");var subQ7=sQuery(id+"F0.wireOp",EDGE,"E1.right");var subQ8=sQuery(id+"F0.wireOp",EDGE,"E1.top");var subQ9=sQuery(id+"F0.wireOp",EDGE,"E1.left");var subQ10=sQuery(id+"F0.wireOp",EDGE,"E23.filletArc");var subQ11=sQuery(id+"F0.wireOp",EDGE,"E24.filletArc");Q0=makeQuery(id+"F2.boolean.opBoolean","SPLIT",FACE,{"disambiguationData":[TD([makeQuery(id+"F1.opExtrude","SWEPT_FACE",FACE,{"disambiguationData":[OSD([subQ6])]})])],"derivedFrom":makeQuery(id+"F1.opExtrude","CAP_FACE",FACE,{"disambiguationData":[OSD([subQ6,subQ8,subQ9,subQ7,subQ4,subQ3,subQ2,subQ1,subQ0,subQ5,subQ10,subQ11])],"isStart":true})});}
            var sketch = newSketch(context, id + "F16", { "sketchPlane" : qUnion([Q0])});
            skLineSegment(sketch, "E79", {"start": v(-32.16, 90) * mm, "end": v(-15, 108) * mm});
            skLineSegment(sketch, "E80", {"start": v(32.58, 90) * mm, "end": v(15, 107.58) * mm});
            skLineSegment(sketch, "E81", {"start": v(0, 90) * mm, "end": v(0, 120) * mm, "construction": true});
            skCircle(sketch, "E82", {"center": v(0, 120) * mm, "radius": 6 * mm});
            skLineSegment(sketch, "E83", {"start": v(-15, 108) * mm, "end": v(-15, 120) * mm});
            skLineSegment(sketch, "E84", {"start": v(15, 107.58) * mm, "end": v(15, 120) * mm});
            skArc(sketch, "E85", {"start": v(15, 120) * mm, "mid": v(0, 135) * mm, "end": v(-15, 120) * mm});
            skLineSegment(sketch, "E86", {"start": v(0, 0) * mm, "end": v(-80, 0) * mm});
            skLineSegment(sketch, "E87", {"start": v(-80, 0) * mm, "end": v(80, 0) * mm, "construction": true});
            skLineSegment(sketch, "E88.MirrorCS", {"start": v(-32.16, -90) * mm, "end": v(-15, -108) * mm});
            skLineSegment(sketch, "E89.MirrorCS", {"start": v(-15, -108) * mm, "end": v(-15, -120) * mm});
            skArc(sketch, "E90.MirrorCS", {"start": v(15, -120) * mm, "mid": v(0, -135) * mm, "end": v(-15, -120) * mm});
            skCircle(sketch, "E91.MirrorC", {"center": v(0, -120) * mm, "radius": 6 * mm});
            skLineSegment(sketch, "E92.MirrorCS", {"start": v(15, -107.58) * mm, "end": v(15, -120) * mm});
            skLineSegment(sketch, "E93.MirrorCS", {"start": v(32.58, -90) * mm, "end": v(15, -107.58) * mm});
            skLineSegment(sketch, "E94.MirrorCS", {"start": v(0, -90) * mm, "end": v(0, -120) * mm, "construction": true});
            skSolve(sketch);
        }
        {
            var Q0;
            {var subQ1=sQuery(id+"F16.wireOp",EDGE,"E79");Q0=makeQuery(id+"F16.imprint","IMPRINT",FACE,{"disambiguationData":[TD([[makeQuery(id+"F16.imprint","IMPRINT",EDGE,{"derivedFrom":subQ1}),-1.0]])]});}
            var Q1;
            Q1=makeQuery(id+"F16.imprint","IMPRINT",FACE,{"disambiguationData":[TD([[makeQuery(id+"F16.imprint","IMPRINT",EDGE,{"derivedFrom":makeQuery(id+"F1.opExtrude","CAP_EDGE",EDGE,{"disambiguationData":[OSD([sQuery(id+"F0.wireOp",EDGE,"E1.right")])],"isStart":true})}),1.0]])]});
            var Q2;
            {var subQ0=sQuery(id+"F16.wireOp",EDGE,"E88.MirrorCS");Q2=makeQuery(id+"F16.imprint","IMPRINT",FACE,{"disambiguationData":[TD([[makeQuery(id+"F16.imprint","IMPRINT",EDGE,{"derivedFrom":subQ0}),1.0]])]});}
            extrude(context, id + "F17", {"entities" : qUnion([Q0, Q1, Q2]), "operationType" : NewBodyOperationType.ADD, "depth" : 25 * mm, "offsetDistance" : 25 * mm});
        }
    });
